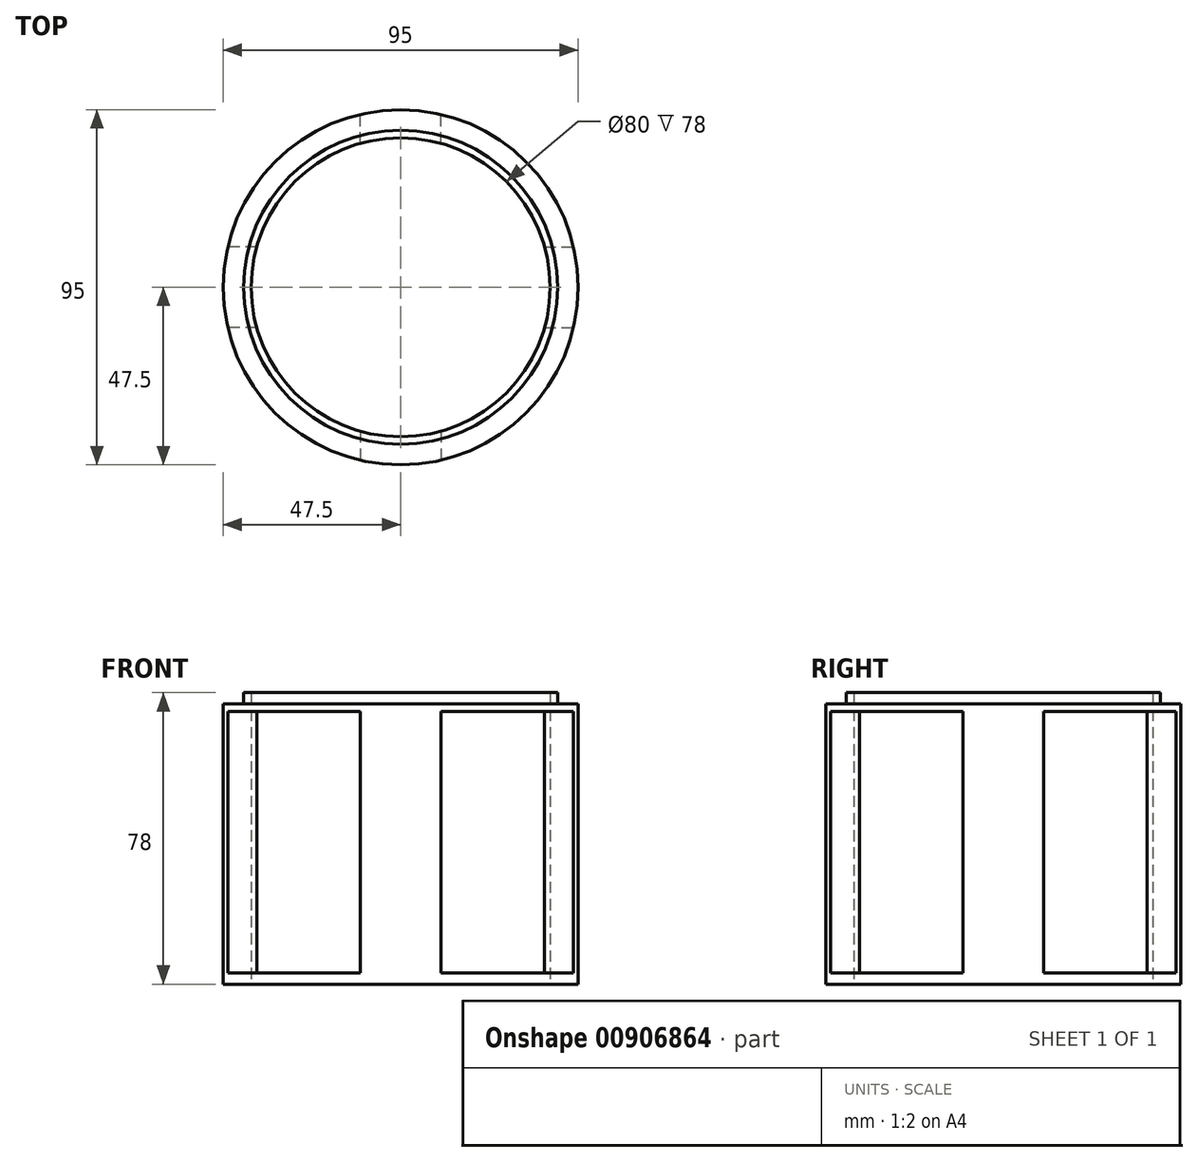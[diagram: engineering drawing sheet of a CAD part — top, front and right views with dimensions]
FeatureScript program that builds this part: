
annotation { "Feature Type Name" : "Feature", "Feature Type Description" : "" }
export const myFeature = defineFeature(function(context is Context, id is Id, definition is map)
    precondition{}
    {
        {
            var Q0;
            Q0=qCreatedBy(makeId("Top.planeOp"),FACE);
            var sketch = newSketch(context, id + "F0", { "sketchPlane" : qUnion([Q0])});
            skCircle(sketch, "E0", {"center": v(0, 0) * mm, "radius": 47.5 * mm});
            skPoint(sketch, "E1.end.orphan", {"position": v(-2.85, -39.9) * mm});
            skPoint(sketch, "E1.start.orphan", {"position": v(-39.9, -2.85) * mm});
            skPoint(sketch, "E2.trimOffspring.end.orphan", {"position": v(-39.9, 2.85) * mm});
            skPoint(sketch, "E2.trimOffspring.start.orphan", {"position": v(-2.85, 39.9) * mm});
            skPoint(sketch, "E3.trimOffspring.end.orphan", {"position": v(2.85, 39.9) * mm});
            skPoint(sketch, "E3.trimOffspring.start.orphan", {"position": v(39.9, 2.85) * mm});
            skPoint(sketch, "E4.trimOffspring.end.orphan", {"position": v(39.9, -2.85) * mm});
            skPoint(sketch, "E4.trimOffspring.start.orphan", {"position": v(2.85, -39.9) * mm});
            skCircle(sketch, "E5", {"center": v(0, 0) * mm, "radius": 40 * mm});
            skSolve(sketch);
        }
        {
            var Q0;
            Q0 = qSketchRegion(id + "F0", true);
            extrude(context, id + "F1", {"entities" : qUnion([Q0]), "depth" : 3 * mm, "offsetDistance" : 25 * mm});
        }
        {
            var Q0;
            Q0=makeQuery(id+"F1.opExtrude","CAP_FACE",FACE,{"disambiguationData":[OSD([sQuery(id+"F0.wireOp",EDGE,"E0"),sQuery(id+"F0.wireOp",EDGE,"E1"),sQuery(id+"F0.wireOp",EDGE,"xVsyM1RN-mjvE-DYux-27Cl-ag5Hct29XK1L.left"),sQuery(id+"F0.wireOp",EDGE,"xVsyM1RN-mjvE-DYux-27Cl-ag5Hct29XK1L.right"),sQuery(id+"F0.wireOp",EDGE,"spzCYwmR-vXFa-KSWS-UBCs-612UuEfsKpsx.bottom"),sQuery(id+"F0.wireOp",EDGE,"spzCYwmR-vXFa-KSWS-UBCs-612UuEfsKpsx.top"),sQuery(id+"F0.wireOp",EDGE,"ba21cf7f-94c6-4ae2-92b5-baf788d1a563.trimOffspring"),sQuery(id+"F0.wireOp",EDGE,"648217c0-c0ce-4180-8910-988510b7371b.trimOffspring"),sQuery(id+"F0.wireOp",EDGE,"a4942edb-ab97-4a85-a6a1-a41fa5f8007c.trimOffspring"),sQuery(id+"F0.wireOp",EDGE,"3a64fc3a-8213-4c07-8854-d6151b9955bf.trimOffspring"),sQuery(id+"F0.wireOp",EDGE,"E3.trimOffspring"),sQuery(id+"F0.wireOp",EDGE,"E2.trimOffspring"),sQuery(id+"F0.wireOp",EDGE,"E4.trimOffspring")])],"isStart":false});
            var sketch = newSketch(context, id + "F2", { "sketchPlane" : qUnion([Q0])});
            skArc(sketch, "E6.0", {"start": v(10.81, 46.25) * mm, "mid": v(0, 47.5) * mm, "end": v(-10.81, 46.25) * mm});
            skArc(sketch, "E7.0", {"start": v(-2.85, 39.9) * mm, "mid": v(-28.28, 28.28) * mm, "end": v(-39.9, 2.85) * mm});
            skLineSegment(sketch, "E8", {"start": v(-10.81, 38.51) * mm, "end": v(-10.81, 46.25) * mm});
            skArc(sketch, "E9", {"start": v(-10.81, 38.51) * mm, "mid": v(-5.46, 39.63) * mm, "end": v(0, 40) * mm});
            skLineSegment(sketch, "E10.MirrorCS", {"start": v(10.81, 38.51) * mm, "end": v(10.81, 46.25) * mm});
            skArc(sketch, "E11.MirrorCS", {"start": v(10.81, 38.51) * mm, "mid": v(5.46, 39.63) * mm, "end": v(0, 40) * mm});
            skArc(sketch, "E12.1.0", {"start": v(-46.25, 10.81) * mm, "mid": v(-47.5, 0) * mm, "end": v(-46.25, -10.81) * mm});
            skArc(sketch, "E12.1.1", {"start": v(-38.51, 10.81) * mm, "mid": v(-39.63, 5.46) * mm, "end": v(-40, 0) * mm});
            skArc(sketch, "E12.1.2", {"start": v(-38.51, -10.81) * mm, "mid": v(-39.63, -5.46) * mm, "end": v(-40, 0) * mm});
            skLineSegment(sketch, "E12.1.3", {"start": v(-38.51, -10.81) * mm, "end": v(-46.25, -10.81) * mm});
            skLineSegment(sketch, "E12.1.4", {"start": v(-38.51, 10.81) * mm, "end": v(-46.25, 10.81) * mm});
            skArc(sketch, "E12.2.0", {"start": v(-10.81, -46.25) * mm, "mid": v(0, -47.5) * mm, "end": v(10.81, -46.25) * mm});
            skArc(sketch, "E12.2.1", {"start": v(-10.81, -38.51) * mm, "mid": v(-5.46, -39.63) * mm, "end": v(0, -40) * mm});
            skArc(sketch, "E12.2.2", {"start": v(10.81, -38.51) * mm, "mid": v(5.46, -39.63) * mm, "end": v(0, -40) * mm});
            skLineSegment(sketch, "E12.2.3", {"start": v(10.81, -38.51) * mm, "end": v(10.81, -46.25) * mm});
            skLineSegment(sketch, "E12.2.4", {"start": v(-10.81, -38.51) * mm, "end": v(-10.81, -46.25) * mm});
            skArc(sketch, "E13.4.3.0", {"start": v(38.51, -10.81) * mm, "mid": v(39.63, -5.46) * mm, "end": v(40, 0) * mm});
            skArc(sketch, "E13.8.3.0", {"start": v(38.51, 10.81) * mm, "mid": v(39.63, 5.46) * mm, "end": v(40, 0) * mm});
            skArc(sketch, "E13.10.3.0", {"start": v(46.25, -10.81) * mm, "mid": v(47.5, 0) * mm, "end": v(46.25, 10.81) * mm});
            skLineSegment(sketch, "E13.12.3.0", {"start": v(38.51, 10.81) * mm, "end": v(46.25, 10.81) * mm});
            skLineSegment(sketch, "E13.15.3.0", {"start": v(38.51, -10.81) * mm, "end": v(46.25, -10.81) * mm});
            skSolve(sketch);
        }
        {
            var Q0;
            Q0 = qSketchRegion(id + "F2", true);
            extrude(context, id + "F3", {"entities" : qUnion([Q0]), "operationType" : NewBodyOperationType.ADD, "depth" : 70 * mm, "offsetDistance" : 25 * mm});
        }
        {
            var Q0;
            Q0=makeQuery(id+"F3.opExtrude","CAP_FACE",FACE,{"disambiguationData":[OSD([sQuery(id+"F2.wireOp",EDGE,"E6.0"),sQuery(id+"F2.wireOp",EDGE,"E8"),sQuery(id+"F2.wireOp",EDGE,"E9"),sQuery(id+"F2.wireOp",EDGE,"E10.MirrorCS"),sQuery(id+"F2.wireOp",EDGE,"E11.MirrorCS")])],"isStart":false});
            var sketch = newSketch(context, id + "F4", { "sketchPlane" : qUnion([Q0])});
            skCircle(sketch, "E14", {"center": v(0, 0) * mm, "radius": 47.5 * mm});
            skCircle(sketch, "E15", {"center": v(0, 0) * mm, "radius": 40 * mm});
            skSolve(sketch);
        }
        {
            var Q0;
            Q0 = qSketchRegion(id + "F4", true);
            extrude(context, id + "F5", {"entities" : qUnion([Q0]), "operationType" : NewBodyOperationType.ADD, "depth" : 2 * mm, "offsetDistance" : 25 * mm});
        }
        {
            var Q0;
            Q0=makeQuery(id+"F5.opExtrude","CAP_FACE",FACE,{"disambiguationData":[OSD([sQuery(id+"F4.wireOp",EDGE,"E14"),sQuery(id+"F4.wireOp",EDGE,"E15")])],"isStart":false});
            var sketch = newSketch(context, id + "F6", { "sketchPlane" : qUnion([Q0])});
            skCircle(sketch, "E16", {"center": v(0, 0) * mm, "radius": 40 * mm});
            skCircle(sketch, "E17", {"center": v(0, 0) * mm, "radius": 42 * mm});
            skSolve(sketch);
        }
        {
            var Q0;
            Q0 = qSketchRegion(id + "F6", true);
            extrude(context, id + "F7", {"entities" : qUnion([Q0]), "operationType" : NewBodyOperationType.ADD, "depth" : 3 * mm, "offsetDistance" : 25 * mm});
        }
    });
